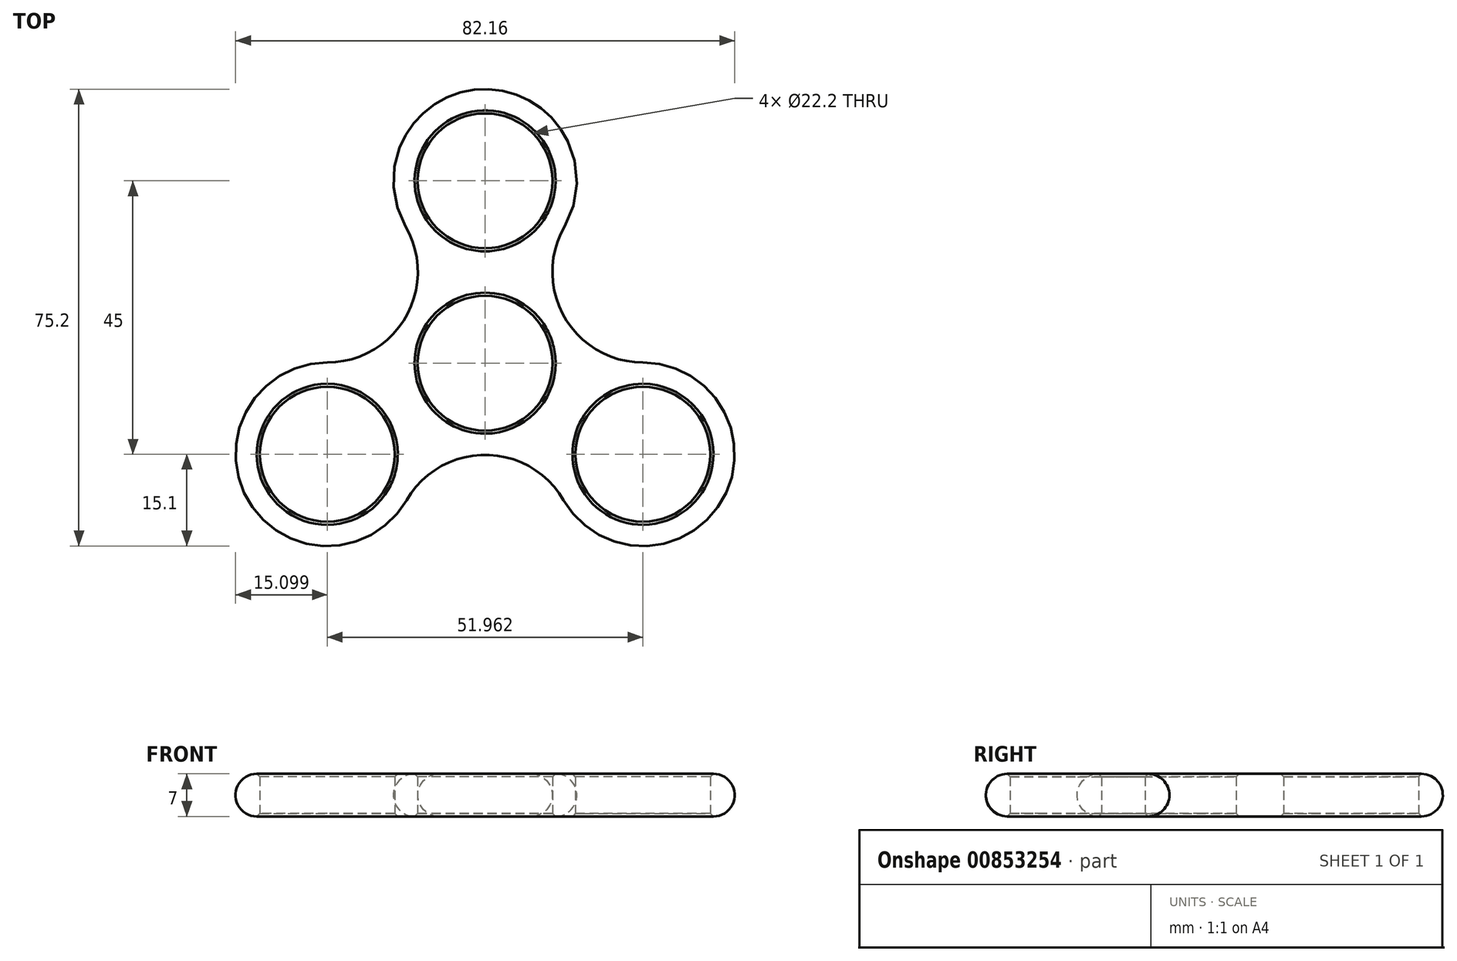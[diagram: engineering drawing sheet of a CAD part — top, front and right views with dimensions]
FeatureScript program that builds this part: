
annotation { "Feature Type Name" : "Feature", "Feature Type Description" : "" }
export const myFeature = defineFeature(function(context is Context, id is Id, definition is map)
    precondition{}
    {
        {
            var Q0;
            Q0=qCreatedBy(makeId("Top.planeOp"),FACE);
            var sketch = newSketch(context, id + "F0", { "sketchPlane" : qUnion([Q0])});
            skCircle(sketch, "E0", {"center": v(0, 0) * mm, "radius": 11.1 * mm});
            skCircle(sketch, "E1", {"center": v(0, 30) * mm, "radius": 11.1 * mm});
            skCircle(sketch, "E2.1.0", {"center": v(-25.98, -15) * mm, "radius": 11.1 * mm});
            skCircle(sketch, "E2.2.0", {"center": v(25.98, -15) * mm, "radius": 11.1 * mm});
            skLineSegment(sketch, "E3", {"start": v(0, 0) * mm, "end": v(-25.98, -15) * mm, "construction": true});
            skLineSegment(sketch, "E4", {"start": v(0, 0) * mm, "end": v(25.98, -15) * mm, "construction": true});
            skLineSegment(sketch, "E5", {"start": v(0, 0) * mm, "end": v(0, 30) * mm, "construction": true});
            skArc(sketch, "E6.0", {"start": v(13.08, 22.45) * mm, "mid": v(0, 45.1) * mm, "end": v(-13.08, 22.45) * mm});
            skArc(sketch, "E7.0", {"start": v(-25.98, 0.1) * mm, "mid": v(-39.06, -22.55) * mm, "end": v(-12.9, -22.55) * mm});
            skArc(sketch, "E8.0", {"start": v(12.9, -22.55) * mm, "mid": v(39.06, -22.55) * mm, "end": v(25.98, 0.1) * mm});
            skLineSegment(sketch, "E9", {"start": v(25.98, -15) * mm, "end": v(25.98, 0.1) * mm, "construction": true});
            skLineSegment(sketch, "E10", {"start": v(-25.98, -15) * mm, "end": v(-25.98, 0.1) * mm, "construction": true});
            skLineSegment(sketch, "E11", {"start": v(0, 30) * mm, "end": v(-13.08, 22.45) * mm, "construction": true});
            skLineSegment(sketch, "E12.MirrorCS", {"start": v(0, 30) * mm, "end": v(13.08, 22.45) * mm, "construction": true});
            skLineSegment(sketch, "E13.MirrorCS", {"start": v(-25.98, -15) * mm, "end": v(-12.9, -22.55) * mm, "construction": true});
            skLineSegment(sketch, "E14.MirrorCS", {"start": v(25.98, -15) * mm, "end": v(12.9, -22.55) * mm, "construction": true});
            skArc(sketch, "E15", {"start": v(-25.98, 0.1) * mm, "mid": v(-13.08, 7.55) * mm, "end": v(-13.08, 22.45) * mm});
            skArc(sketch, "E16", {"start": v(13.08, 22.45) * mm, "mid": v(13.08, 7.55) * mm, "end": v(25.98, 0.1) * mm});
            skArc(sketch, "E17", {"start": v(12.9, -22.55) * mm, "mid": v(0, -15.1) * mm, "end": v(-12.9, -22.55) * mm});
            skSolve(sketch);
        }
        {
            var Q0;
            Q0=makeQuery(id+"F0.imprint","IMPRINT",FACE,{"disambiguationData":[TD([[makeQuery(id+"F0.imprint","IMPRINT",EDGE,{"derivedFrom":sQuery(id+"F0.wireOp",EDGE,"E0")}),-1.0]])]});
            extrude(context, id + "F1", {"entities" : qUnion([Q0]), "depth" : 7 * mm, "offsetDistance" : 25 * mm});
        }
        {
            var Q0;
            Q0=makeQuery(id+"F1.opExtrude","CAP_EDGE",EDGE,{"disambiguationData":[OSD([sQuery(id+"F0.wireOp",EDGE,"E17")])],"isStart":false});
            var Q1;
            Q1=makeQuery(id+"F1.opExtrude","CAP_EDGE",EDGE,{"disambiguationData":[OSD([sQuery(id+"F0.wireOp",EDGE,"E17")])],"isStart":true});
            fillet(context, id + "F2", {"entities" : qUnion([Q0, Q1]), "radius" : 3.5 * mm, "tangentPropagation" : true, "allowEdgeOverflow" : false});
        }
        {
            var Q0;
            Q0=makeQuery(id+"F1.opExtrude","CAP_EDGE",EDGE,{"disambiguationData":[OSD([sQuery(id+"F0.wireOp",EDGE,"E1")])],"isStart":false});
            var Q1;
            Q1=makeQuery(id+"F1.opExtrude","CAP_EDGE",EDGE,{"disambiguationData":[OSD([sQuery(id+"F0.wireOp",EDGE,"E0")])],"isStart":false});
            var Q2;
            Q2=makeQuery(id+"F1.opExtrude","CAP_EDGE",EDGE,{"disambiguationData":[OSD([sQuery(id+"F0.wireOp",EDGE,"E2.1.0")])],"isStart":false});
            var Q3;
            Q3=makeQuery(id+"F1.opExtrude","CAP_EDGE",EDGE,{"disambiguationData":[OSD([sQuery(id+"F0.wireOp",EDGE,"E2.2.0")])],"isStart":false});
            var Q4;
            Q4=makeQuery(id+"F1.opExtrude","CAP_EDGE",EDGE,{"disambiguationData":[OSD([sQuery(id+"F0.wireOp",EDGE,"E1")])],"isStart":true});
            var Q5;
            Q5=makeQuery(id+"F1.opExtrude","CAP_EDGE",EDGE,{"disambiguationData":[OSD([sQuery(id+"F0.wireOp",EDGE,"E2.1.0")])],"isStart":true});
            var Q6;
            Q6=makeQuery(id+"F1.opExtrude","CAP_EDGE",EDGE,{"disambiguationData":[OSD([sQuery(id+"F0.wireOp",EDGE,"E0")])],"isStart":true});
            var Q7;
            Q7=makeQuery(id+"F1.opExtrude","CAP_EDGE",EDGE,{"disambiguationData":[OSD([sQuery(id+"F0.wireOp",EDGE,"E2.2.0")])],"isStart":true});
            chamfer(context, id + "F3", {"entities" : qUnion([Q0, Q1, Q2, Q3, Q4, Q5, Q6, Q7]), "width" : 0.5 * mm});
        }
    });
